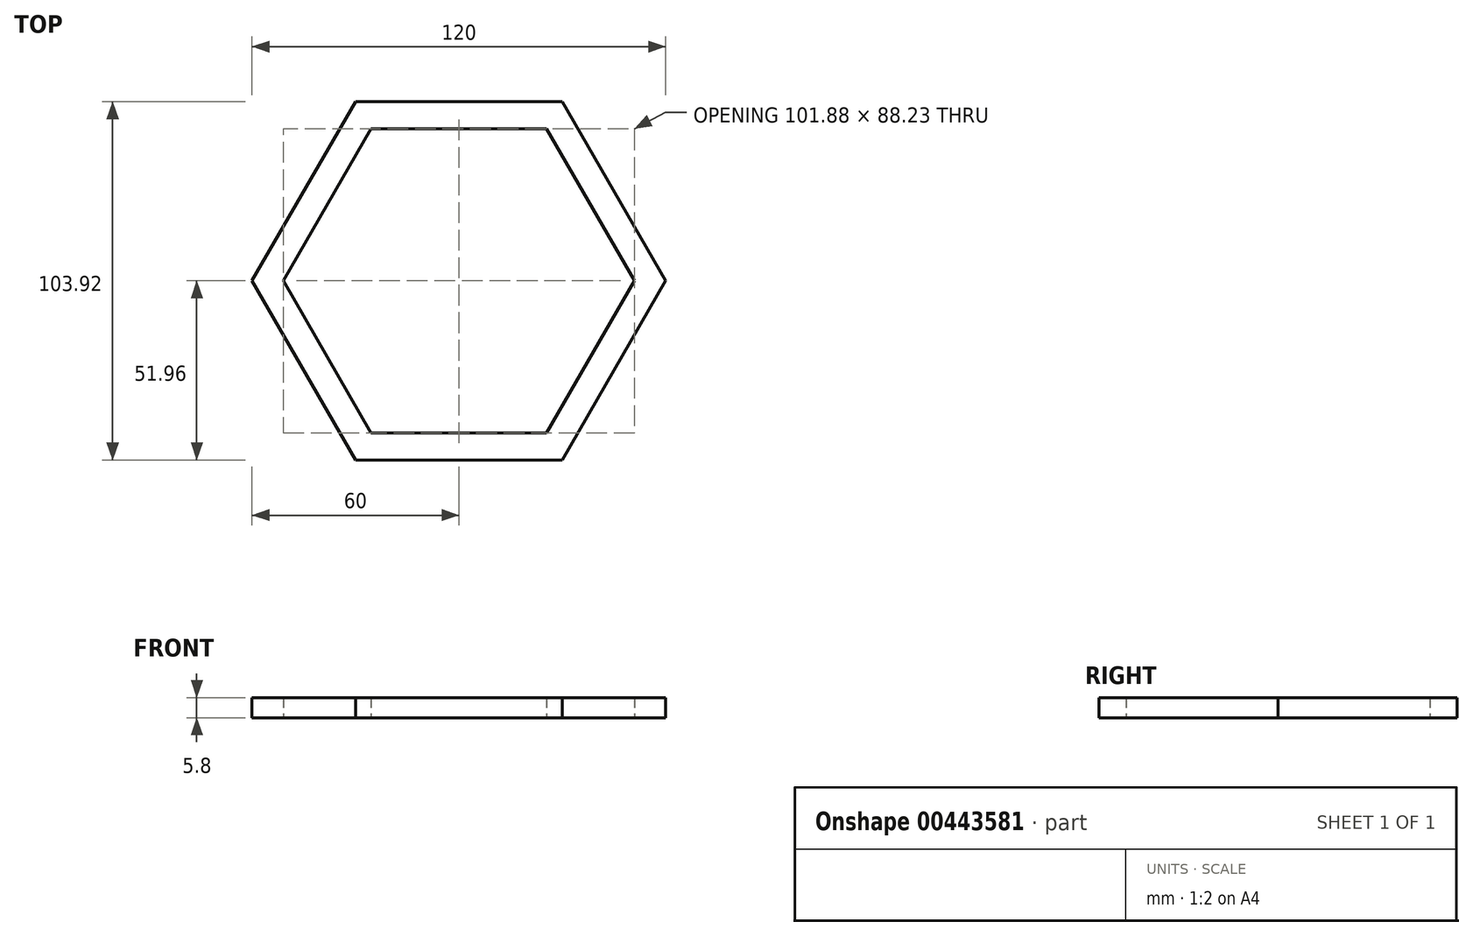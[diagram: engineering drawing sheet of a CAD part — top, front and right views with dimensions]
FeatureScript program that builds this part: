
annotation { "Feature Type Name" : "Feature", "Feature Type Description" : "" }
export const myFeature = defineFeature(function(context is Context, id is Id, definition is map)
    precondition{}
    {
        {
            var Q0;
            Q0=qCreatedBy(makeId("Top.planeOp"),FACE);
            var sketch = newSketch(context, id + "F0", { "sketchPlane" : qUnion([Q0])});
            skLineSegment(sketch, "E0", {"start": v(-25.47, 44.12) * mm, "end": v(-50.94, 0) * mm});
            skLineSegment(sketch, "E1", {"start": v(25.47, 44.12) * mm, "end": v(50.94, 0) * mm});
            skLineSegment(sketch, "E2", {"start": v(-50.94, 0) * mm, "end": v(-25.47, -44.12) * mm});
            skLineSegment(sketch, "E3", {"start": v(50.94, 0) * mm, "end": v(25.47, -44.12) * mm});
            skLineSegment(sketch, "E4", {"start": v(25.47, -44.12) * mm, "end": v(-25.47, -44.12) * mm});
            skCircle(sketch, "E5", {"center": v(0, 0) * mm, "radius": 44.12 * mm, "construction": true});
            skLineSegment(sketch, "E6", {"start": v(-25.47, 44.12) * mm, "end": v(25.47, 44.12) * mm});
            skLineSegment(sketch, "E7", {"start": v(-30, 51.96) * mm, "end": v(-60, 0) * mm});
            skLineSegment(sketch, "E8", {"start": v(30, 51.96) * mm, "end": v(60, 0) * mm});
            skLineSegment(sketch, "E9", {"start": v(-60, 0) * mm, "end": v(-30, -51.96) * mm});
            skLineSegment(sketch, "E10", {"start": v(60, 0) * mm, "end": v(30, -51.96) * mm});
            skLineSegment(sketch, "E11", {"start": v(30, -51.96) * mm, "end": v(-30, -51.96) * mm});
            skCircle(sketch, "E12", {"center": v(0, 0) * mm, "radius": 51.96 * mm, "construction": true});
            skLineSegment(sketch, "E13", {"start": v(-30, 51.96) * mm, "end": v(30, 51.96) * mm});
            skSolve(sketch);
        }
        {
            var Q0;
            Q0=makeQuery(id+"F0.imprint","IMPRINT",FACE,{"disambiguationData":[TD([[makeQuery(id+"F0.imprint","IMPRINT",EDGE,{"derivedFrom":sQuery(id+"F0.wireOp",EDGE,"E0")}),-1.0]])]});
            extrude(context, id + "F1", {"entities" : qUnion([Q0]), "depth" : 5.8 * mm});
        }
    });
